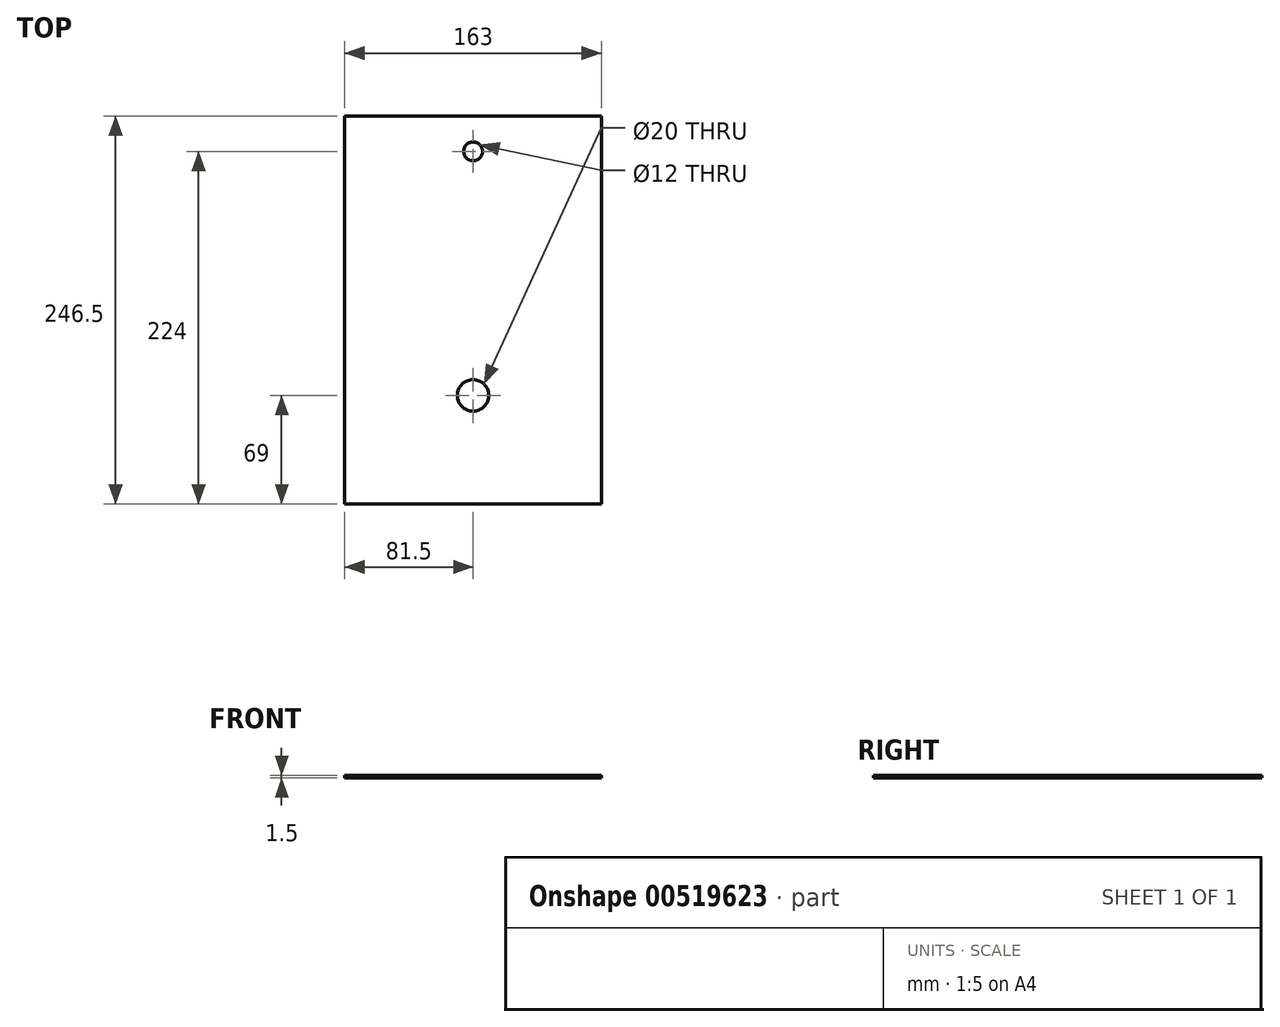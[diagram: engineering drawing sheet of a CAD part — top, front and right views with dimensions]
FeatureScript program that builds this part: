
annotation { "Feature Type Name" : "Feature", "Feature Type Description" : "" }
export const myFeature = defineFeature(function(context is Context, id is Id, definition is map)
    precondition{}
    {
        {
            var Q0;
            Q0=qCreatedBy(makeId("Top.planeOp"),FACE);
            var sketch = newSketch(context, id + "F0", { "sketchPlane" : qUnion([Q0])});
            skLineSegment(sketch, "E0.bottom", {"start": v(81.5, 123.25) * mm, "end": v(-81.5, 123.25) * mm});
            skLineSegment(sketch, "E0.top", {"start": v(81.5, -123.25) * mm, "end": v(-81.5, -123.25) * mm});
            skLineSegment(sketch, "E0.left", {"start": v(81.5, 123.25) * mm, "end": v(81.5, -123.25) * mm});
            skLineSegment(sketch, "E0.right", {"start": v(-81.5, 123.25) * mm, "end": v(-81.5, -123.25) * mm});
            skPoint(sketch, "E0.middle", {"position": v(0, 0) * mm});
            skSolve(sketch);
        }
        {
            var Q0;
            Q0 = qSketchRegion(id + "F0", true);
            extrude(context, id + "F1", {"entities" : qUnion([Q0]), "depth" : 1.5 * mm, "offsetDistance" : 25 * mm});
        }
        {
            var Q0;
            Q0=makeQuery(id+"F1.opExtrude","CAP_FACE",FACE,{"disambiguationData":[OSD([sQuery(id+"F0.wireOp",EDGE,"E0.bottom"),sQuery(id+"F0.wireOp",EDGE,"E0.top"),sQuery(id+"F0.wireOp",EDGE,"E0.left"),sQuery(id+"F0.wireOp",EDGE,"E0.right")])],"isStart":false});
            var sketch = newSketch(context, id + "F2", { "sketchPlane" : qUnion([Q0])});
            skCircle(sketch, "E1", {"center": v(0, 100.75) * mm, "radius": 6 * mm});
            skPoint(sketch, "E1.centerSnap0", {"position": v(0, 123.25) * mm});
            skCircle(sketch, "E2", {"center": v(0, -54.25) * mm, "radius": 10 * mm});
            skSolve(sketch);
        }
        {
            var Q0;
            Q0 = qSketchRegion(id + "F2", true);
            extrude(context, id + "F3", {"entities" : qUnion([Q0]), "operationType" : NewBodyOperationType.REMOVE, "oppositeDirection" : true, "depth" : 1.5 * mm, "offsetDistance" : 25 * mm});
        }
    });
